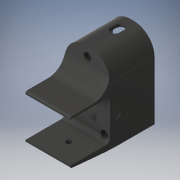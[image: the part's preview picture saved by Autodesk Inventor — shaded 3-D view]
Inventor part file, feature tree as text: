
AUTODESK INVENTOR PART (.ipt)
format: ipt  version: 2019.4 (Build 234330000, 330)  size: 276,480 bytes
history: native  units: mm
features: fillet x7, sketch x4, extrude x4, hole x3, other x2, loft x1
ambient origin geometry x8: Origin, YZ Plane, XZ Plane, XY Plane, X Axis, Y Axis, Z Axis, Center Point
bodies: Solid1 (feature_tree)
feature tree (21):
  sketch  "Sketch1"  dims[d0=40.0mm d1=74.8mm]
  extrude  "Extrusion1"  Depth=74.8mm
  extrude  "Extrusion2"  Depth=17.0mm
  hole  "Hole1"  [1 undecoded]
  extrude  "Extrusion3"  Depth=9.0mm
  fillet  "Fillet1"  Radius=15.0mm
  fillet  "Fillet2"  Radius=45.0mm
  fillet  "Fillet3"  Radius=79.8mm
  fillet  "Fillet4"  Radius=45.0mm
  loft  "Loft1"
  fillet  "Fillet5"  Radius=20.0mm
  fillet  "Fillet6"  Radius=45.0mm
  hole  "Hole2"  [1 undecoded]
  hole  "Hole3"  [1 undecoded]
  fillet  "Fillet7"  Radius=2.5mm
  extrude  "Extrusion4"  Depth=9.0mm TaperAngle=0.0deg
  other  "Edges1"
  other  "Edges2"
  sketch  "Sketch2"  dims[d2=34.0mm d3=17.0mm]
  sketch  "Sketch3"  dims[d4=8.426mm d5=8.426mm]
  sketch  "Sketch4"  dims[d6=17.5mm d7=17.5mm d8=15.0mm d9=45.0mm d10=79.8mm d11=45.0mm d12=7.0mm d13=20.0mm d14=0.0mm d15=45.0mm d16=0.0mm d17=4.134mm d18=10.0mm d19=7.5mm d20=4.0mm d21=90.0deg d22=14.2mm d23=20.594885mm d24=45.0mm d25=2.5mm d26=2.5mm d27=40.0mm d28=0.0mm d29=6.0mm d30=21.0mm d31=21.0mm d32=17.0mm d33=0.0mm d34=90.0deg d35=0.0mm d36=90.0deg d37=250.0mm d38=2.0mm d39=40.0mm d40=3.5mm d41=5.0mm d42=10.0mm d43=7.5mm d44=4.0mm d45=90.0deg d46=14.2mm d47=20.594885mm d48=8.0mm d49=9.0mm d50=6.5mm d51=10.0mm d52=7.5mm d53=4.0mm d54=90.0deg d55=14.2mm d56=20.594885mm d57=4.0mm d58=25.0mm d59=9.981mm d60=2.5mm d61=9.0mm d62=40.0mm d63=0.0mm]
note: 3 required parameter values undecoded (feature->parameter linkage not recoverable at this tier; creation-order binding heuristic only, values carry confidence <= 0.55)
